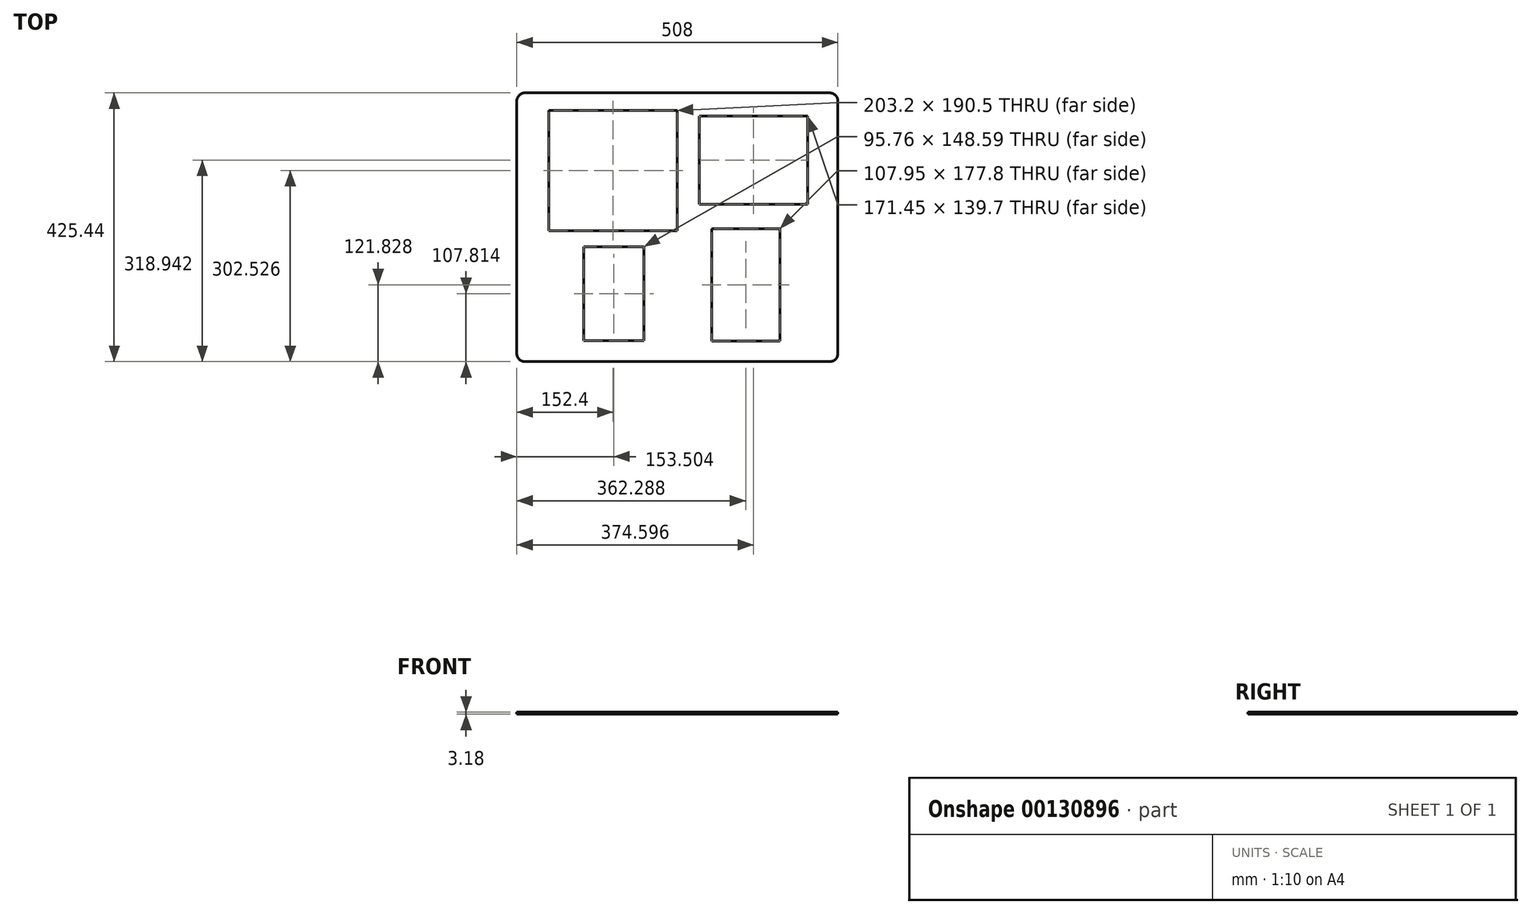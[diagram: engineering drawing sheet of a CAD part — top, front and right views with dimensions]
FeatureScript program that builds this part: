
annotation { "Feature Type Name" : "Feature", "Feature Type Description" : "" }
export const myFeature = defineFeature(function(context is Context, id is Id, definition is map)
    precondition{}
    {
        {
            var Q0;
            Q0=qCreatedBy(makeId("Top.planeOp"),FACE);
            var sketch = newSketch(context, id + "F0", { "sketchPlane" : qUnion([Q0])});
            skLineSegment(sketch, "E0.bottom", {"start": v(241.3, 212.73) * mm, "end": v(-241.3, 212.73) * mm});
            skLineSegment(sketch, "E0.top", {"start": v(241.3, -212.73) * mm, "end": v(-241.3, -212.73) * mm});
            skLineSegment(sketch, "E0.left", {"start": v(254, 200.03) * mm, "end": v(254, -200.03) * mm});
            skLineSegment(sketch, "E0.right", {"start": v(-254, 200.02) * mm, "end": v(-254, -200.03) * mm});
            skPoint(sketch, "E0.middle", {"position": v(0, 0) * mm});
            skPoint(sketch, "E1.visualSharp", {"position": v(-254, 212.73) * mm});
            skArc(sketch, "E1.filletArc", {"start": v(-241.3, 212.72) * mm, "mid": v(-250.28, 209) * mm, "end": v(-254, 200.02) * mm});
            skPoint(sketch, "E2.visualSharp", {"position": v(-254, -212.73) * mm});
            skArc(sketch, "E2.filletArc", {"start": v(-254, -200.03) * mm, "mid": v(-250.28, -209) * mm, "end": v(-241.3, -212.73) * mm});
            skPoint(sketch, "E3.visualSharp", {"position": v(254, -212.73) * mm});
            skArc(sketch, "E3.filletArc", {"start": v(241.3, -212.73) * mm, "mid": v(250.28, -209) * mm, "end": v(254, -200.03) * mm});
            skPoint(sketch, "E4.visualSharp", {"position": v(254, 212.73) * mm});
            skArc(sketch, "E4.filletArc", {"start": v(254, 200.03) * mm, "mid": v(250.28, 209) * mm, "end": v(241.3, 212.73) * mm});
            skSolve(sketch);
        }
        {
            var Q0;
            Q0=makeQuery(id+"F0.imprint","IMPRINT",FACE,{"disambiguationData":[TD([[makeQuery(id+"F0.imprint","IMPRINT",EDGE,{"derivedFrom":sQuery(id+"F0.wireOp",EDGE,"E0.bottom")}),1.0]])]});
            extrude(context, id + "F1", {"entities" : qUnion([Q0]), "depth" : 3.17 * mm});
        }
        {
            var Q0;
            Q0=makeQuery(id+"F1.opExtrude","CAP_FACE",FACE,{"disambiguationData":[OSD([sQuery(id+"F0.wireOp",EDGE,"E0.bottom"),sQuery(id+"F0.wireOp",EDGE,"E0.top"),sQuery(id+"F0.wireOp",EDGE,"E0.left"),sQuery(id+"F0.wireOp",EDGE,"E0.right"),sQuery(id+"F0.wireOp",EDGE,"E1.filletArc"),sQuery(id+"F0.wireOp",EDGE,"E2.filletArc"),sQuery(id+"F0.wireOp",EDGE,"E3.filletArc"),sQuery(id+"F0.wireOp",EDGE,"E4.filletArc")])],"isStart":false});
            var sketch = newSketch(context, id + "F2", { "sketchPlane" : qUnion([Q0])});
            skLineSegment(sketch, "E5.bottom", {"start": v(-148.38, -30.61) * mm, "end": v(-52.62, -30.61) * mm});
            skLineSegment(sketch, "E5.top", {"start": v(-148.38, -179.2) * mm, "end": v(-52.62, -179.2) * mm});
            skLineSegment(sketch, "E5.left", {"start": v(-148.38, -30.61) * mm, "end": v(-148.38, -179.2) * mm});
            skLineSegment(sketch, "E5.right", {"start": v(-52.62, -30.61) * mm, "end": v(-52.62, -179.2) * mm});
            skLineSegment(sketch, "E6.bottom", {"start": v(54.31, -2) * mm, "end": v(162.26, -2) * mm});
            skLineSegment(sketch, "E6.top", {"start": v(54.31, -179.8) * mm, "end": v(162.26, -179.8) * mm});
            skLineSegment(sketch, "E6.left", {"start": v(54.31, -2) * mm, "end": v(54.31, -179.8) * mm});
            skLineSegment(sketch, "E6.right", {"start": v(162.26, -2) * mm, "end": v(162.26, -179.8) * mm});
            skLineSegment(sketch, "E7.bottom", {"start": v(-203.2, 185.06) * mm, "end": v(0, 185.06) * mm});
            skLineSegment(sketch, "E7.top", {"start": v(-203.2, -5.44) * mm, "end": v(0, -5.44) * mm});
            skLineSegment(sketch, "E7.left", {"start": v(-203.2, 185.06) * mm, "end": v(-203.2, -5.44) * mm});
            skLineSegment(sketch, "E7.right", {"start": v(0, 185.06) * mm, "end": v(0, -5.44) * mm});
            skLineSegment(sketch, "E8.bottom", {"start": v(34.87, 176.07) * mm, "end": v(206.32, 176.07) * mm});
            skLineSegment(sketch, "E8.top", {"start": v(34.87, 36.37) * mm, "end": v(206.32, 36.37) * mm});
            skLineSegment(sketch, "E8.left", {"start": v(34.87, 176.07) * mm, "end": v(34.87, 36.37) * mm});
            skLineSegment(sketch, "E8.right", {"start": v(206.32, 176.07) * mm, "end": v(206.32, 36.37) * mm});
            skSolve(sketch);
        }
        {
            var Q0;
            Q0=makeQuery(id+"F2.imprint","IMPRINT",FACE,{"disambiguationData":[TD([[makeQuery(id+"F2.imprint","IMPRINT",EDGE,{"derivedFrom":sQuery(id+"F2.wireOp",EDGE,"E7.bottom")}),-1.0]])]});
            var Q1;
            Q1=makeQuery(id+"F2.imprint","IMPRINT",FACE,{"disambiguationData":[TD([[makeQuery(id+"F2.imprint","IMPRINT",EDGE,{"derivedFrom":sQuery(id+"F2.wireOp",EDGE,"E5.bottom")}),-1.0]])]});
            var Q2;
            Q2=makeQuery(id+"F2.imprint","IMPRINT",FACE,{"disambiguationData":[TD([[makeQuery(id+"F2.imprint","IMPRINT",EDGE,{"derivedFrom":sQuery(id+"F2.wireOp",EDGE,"E6.bottom")}),-1.0]])]});
            var Q3;
            Q3=makeQuery(id+"F2.imprint","IMPRINT",FACE,{"disambiguationData":[TD([[makeQuery(id+"F2.imprint","IMPRINT",EDGE,{"derivedFrom":sQuery(id+"F2.wireOp",EDGE,"E8.bottom")}),-1.0]])]});
            extrude(context, id + "F3", {"entities" : qUnion([Q0, Q1, Q2, Q3]), "operationType" : NewBodyOperationType.REMOVE, "oppositeDirection" : true, "depth" : 25.4 * mm});
        }
    });
